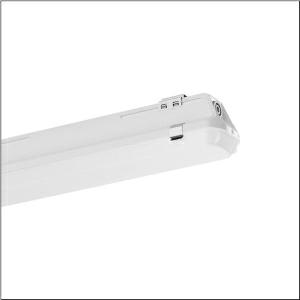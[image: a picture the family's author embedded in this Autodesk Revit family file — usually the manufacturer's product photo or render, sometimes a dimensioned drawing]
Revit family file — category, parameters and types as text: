
# Revit family: monsun_21_51fb107p480c
name_source: partatom
category: Lighting Fixtures
units: mm (PartAtom-declared; Revit-internal decimal feet)

## family parameters
Cut with Voids When Loaded = No
Host = Face
Light Source = No
Part Type = Normal
Room Calculation Point = No
Round Connector Dimension = Use Diameter
Shared = No

## types (1)
- Monsun 21 (1 x LED, 8070 lm, 44.5 W, 4000K)
    Apparent Load = 45 VA
    CIE Flux Codes = 47 77 93 94 100
    Color Rendering = 80
    Color Temperature = 4000K
    Default Elevation = 1800 mm
    Description = Monsun 21, damp-proof luminaire, chain hanger, primary optical cover: enclosure, of PMMA, light emission: direct distribution, primary light characteristic: symmetric, installation type: suspended mounting, surface-mounted, horizontal mounting, vertical mounting, LED, rated luminous flux: 8.070lm, luminous efficacy: 181lm/W, light colour: 840, colour temperature: 4000K, control gear: ON/OFF, with terminal, 3-pole, max. 2.5mm², mains connection: 220..240V, AC, 50/60Hz, rated input power: 45W, housing, of glass-fibre reinforced polyester, uncoated, bright grey, incl. chain hanger, length: 1.590mm, width: 90mm, height: 88mm, clip for enclosure, of stainless steel (V2A), ceiling mounting element, of stainless steel (V2A), chain hanger, of stainless steel (V2A), protection rating (complete): IP66, insulation class (complete): insulation class I (protective earthing), certification: CE, ENEC, VDE, UKCA, protection symbol: D, impact resistance: IK04, permissible operating ambient temperature: -25..+35°C, standard: EN 50419, EN 60598-2-1, corresponds to IFS (International Featured Standards) requirements for safety and quality in the food industry, for indoor or canopied outdoor use, no direct snow, no direct sun, no direct rain, LABS conformity tested according to VDMA 24364:2018-05, contact your sales advisor before using the luminaires in applications with unclear chemical exposure, large temperature fluctuations or condensation-forming humidity, packaging unit: 1 piece
    Height = 89 mm
    Lamp = 1 x LED
    Lamp Light Flux = 8070 lm
    Lamp Power = 44.5 W
    Lamp count = 1
    Length = 1590 mm
    Luminous efficacy = 181 lm/W
    Manufacturer = Siteco
    ModVariant = No
    Model = 51FB107P480C
    Mounting Place = Ceiling
    Mounting Type = Surface mounted
    Number of Poles = 1
    OnlyDefault = Yes
    Power Factor = 1
    Product Name = Monsun 21
    Product group = damp-proof luminaire
    ProductGroupID = 300
    Protection Class = Protection class I
    Protection Degree = IP 66
    RLX_Detail_Level = 1
    RLX_Emergency_Light_Flux = 0 lm
    RLX_Emergency_Type = 0
    RLX_Emergency_Type_DB = No
    RlxData = <blob elided: 88405 chars, md5=b0dfd961>
    Socket = socket
    Standby Power = 0 W
    System Light Flux = 8070 lm
    System Power = 45 W
    Type Comments = Product without accessories
    Type Image = l_1319656.jpg
    URL = http://relux.com
    VarID = ---
    Voltage = 0 V
    Weight = 0.00 kg
    Width = 90 mm

## geometry (parser evidence)
native form markers: Blend x4, Sweep x11
no freeform markers — native parametric forms only
